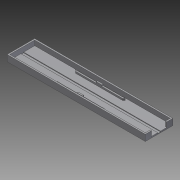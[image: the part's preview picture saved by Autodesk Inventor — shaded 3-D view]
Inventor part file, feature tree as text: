
AUTODESK INVENTOR PART (.ipt)
format: ipt  version: 2011 (Build 150239000, 239)  size: 155,136 bytes
history: native  units: mm
features: sketch x6, extrude x4, other x2, imported_body x1, hole x1, mirror x1
ambient origin geometry x8: Origin, YZ Plane, XZ Plane, XY Plane, X Axis, Y Axis, Z Axis, Center Point
feature tree (15):
  imported_body  "Base"
  other  "Sólido1"
  extrude  "Canal"  Depth=40.0mm
  extrude  "Paredes"  Depth=4.0mm
  other  "Mitad"
  hole  "Hole1"  [1 undecoded]
  extrude  "Extrusión4"  Depth=2.0mm
  extrude  "Extrusión5"  Depth=2.0mm
  mirror  "Simetría1"
  sketch  "Boceto1"  dims[d0=200.0mm d1=40.0mm]
  sketch  "Boceto2"  dims[d2=2.0mm d3=0.0mm d4=4.0mm]
  sketch  "Boceto3"  dims[d5=2.0mm d6=1.0mm d7=0.0mm]
  sketch  "Boceto4"  dims[d8=2.0mm d9=2.0mm]
  sketch  "Boceto5"  dims[d10=2.0mm d11=2.0mm]
  sketch  "Boceto6"  dims[d12=2.0mm d13=7.0mm d14=0.0mm d15=1.0mm d16=6.0mm d17=4.0mm d18=2.0mm d19=90.0deg d20=8.0mm d21=20.594885mm d23=2.0mm d24=2.0mm d25=3.0mm d26=62.0mm d28=2.5mm d29=0.0mm d30=8.0mm d31=2.0mm d32=0.0mm d33=7.0mm d34=7.0mm d35=62.0mm d36=4.3mm d37=4.3mm d38=49.0mm d39=48.5mm]
note: 1 required parameter value undecoded (feature->parameter linkage not recoverable at this tier; creation-order binding heuristic only, values carry confidence <= 0.55)
